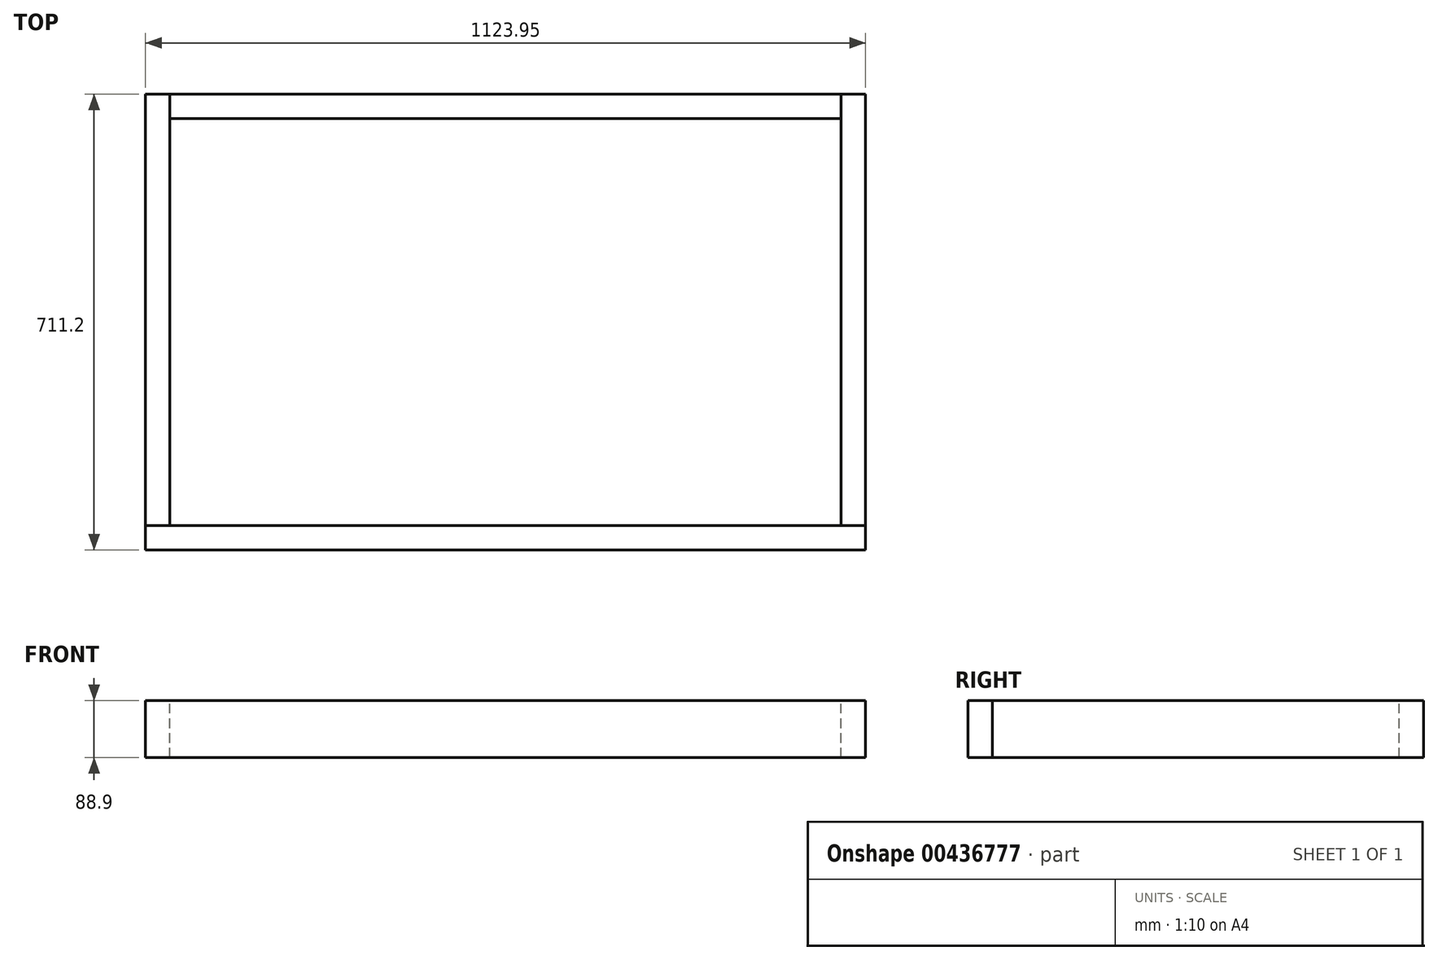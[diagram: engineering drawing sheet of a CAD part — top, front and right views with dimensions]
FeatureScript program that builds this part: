
annotation { "Feature Type Name" : "Feature", "Feature Type Description" : "" }
export const myFeature = defineFeature(function(context is Context, id is Id, definition is map)
    precondition{}
    {
        {
            var Q0;
            Q0=qCreatedBy(makeId("Front.planeOp"),FACE);
            var sketch = newSketch(context, id + "F0", { "sketchPlane" : qUnion([Q0])});
            skLineSegment(sketch, "E0.bottom", {"start": v(0, 0) * mm, "end": v(38.1, 0) * mm});
            skLineSegment(sketch, "E0.top", {"start": v(0, 88.9) * mm, "end": v(38.1, 88.9) * mm});
            skLineSegment(sketch, "E0.left", {"start": v(0, 0) * mm, "end": v(0, 88.9) * mm});
            skLineSegment(sketch, "E0.right", {"start": v(38.1, 0) * mm, "end": v(38.1, 88.9) * mm});
            skSolve(sketch);
        }
        {
            var Q0;
            Q0 = qSketchRegion(id + "F0", true);
            extrude(context, id + "F1", {"entities" : qUnion([Q0]), "oppositeDirection" : true, "depth" : 673.1 * mm});
        }
        {
            var Q0;
            Q0=makeQuery(id+"F1.opExtrude","SWEPT_FACE",FACE,{"disambiguationData":[OSD([sQuery(id+"F0.wireOp",EDGE,"E0.left")])]});
            var sketch = newSketch(context, id + "F2", { "sketchPlane" : qUnion([Q0])});
            skLineSegment(sketch, "E1.bottom", {"start": v(-673.1, 0) * mm, "end": v(-635, 0) * mm});
            skLineSegment(sketch, "E1.top", {"start": v(-673.1, 88.9) * mm, "end": v(-635, 88.9) * mm});
            skLineSegment(sketch, "E1.left", {"start": v(-673.1, 0) * mm, "end": v(-673.1, 88.9) * mm});
            skLineSegment(sketch, "E1.right", {"start": v(-635, 0) * mm, "end": v(-635, 88.9) * mm});
            skSolve(sketch);
        }
        {
            var Q0;
            Q0=makeQuery(id+"F2.imprint","IMPRINT",FACE,{"disambiguationData":[TD([[makeQuery(id+"F2.imprint","IMPRINT",EDGE,{"derivedFrom":sQuery(id+"F2.wireOp",EDGE,"E1.bottom")}),1.0]])]});
            extrude(context, id + "F3", {"entities" : qUnion([Q0]), "depth" : 1047.75 * mm});
        }
        {
            var Q0;
            Q0=makeQuery(id+"F3.opExtrude","SWEPT_FACE",FACE,{"disambiguationData":[OSD([sQuery(id+"F2.wireOp",EDGE,"E1.left")])]});
            var sketch = newSketch(context, id + "F4", { "sketchPlane" : qUnion([Q0])});
            skLineSegment(sketch, "E2.bottom", {"start": v(1047.75, 0) * mm, "end": v(1085.85, 0) * mm});
            skLineSegment(sketch, "E2.top", {"start": v(1047.75, 88.9) * mm, "end": v(1085.85, 88.9) * mm});
            skLineSegment(sketch, "E2.left", {"start": v(1047.75, 0) * mm, "end": v(1047.75, 88.9) * mm});
            skLineSegment(sketch, "E2.right", {"start": v(1085.85, 0) * mm, "end": v(1085.85, 88.9) * mm});
            skSolve(sketch);
        }
        {
            var Q0;
            Q0 = qSketchRegion(id + "F4", true);
            var Q1;
            Q1=makeQuery(id+"F1.opExtrude","CAP_FACE",FACE,{"disambiguationData":[OSD([sQuery(id+"F0.wireOp",EDGE,"E0.bottom"),sQuery(id+"F0.wireOp",EDGE,"E0.top"),sQuery(id+"F0.wireOp",EDGE,"E0.left"),sQuery(id+"F0.wireOp",EDGE,"E0.right")])],"isStart":true});
            extrude(context, id + "F5", {"entities" : qUnion([Q0]), "endBound" : BoundingType.UP_TO_SURFACE, "oppositeDirection" : true, "endBoundEntityFace" : qUnion([Q1]), "depth" : 25.4 * mm});
        }
        {
            var Q0;
            Q0=makeQuery(id+"F1.opExtrude","SWEPT_FACE",FACE,{"disambiguationData":[OSD([sQuery(id+"F0.wireOp",EDGE,"E0.right")])]});
            var sketch = newSketch(context, id + "F6", { "sketchPlane" : qUnion([Q0])});
            skLineSegment(sketch, "E3.bottom", {"start": v(0, 0) * mm, "end": v(-38.1, 0) * mm});
            skLineSegment(sketch, "E3.top", {"start": v(0, 88.9) * mm, "end": v(-38.1, 88.9) * mm});
            skLineSegment(sketch, "E3.left", {"start": v(0, 0) * mm, "end": v(0, 88.9) * mm});
            skLineSegment(sketch, "E3.right", {"start": v(-38.1, 0) * mm, "end": v(-38.1, 88.9) * mm});
            skSolve(sketch);
        }
        {
            var Q0;
            Q0 = qSketchRegion(id + "F6", true);
            var Q1;
            Q1=makeQuery(id+"F5.opExtrude","SWEPT_FACE",FACE,{"disambiguationData":[OSD([sQuery(id+"F4.wireOp",EDGE,"E2.right")])]});
            extrude(context, id + "F7", {"entities" : qUnion([Q0]), "endBound" : BoundingType.UP_TO_SURFACE, "oppositeDirection" : true, "endBoundEntityFace" : qUnion([Q1]), "depth" : 25.4 * mm});
        }
    });
